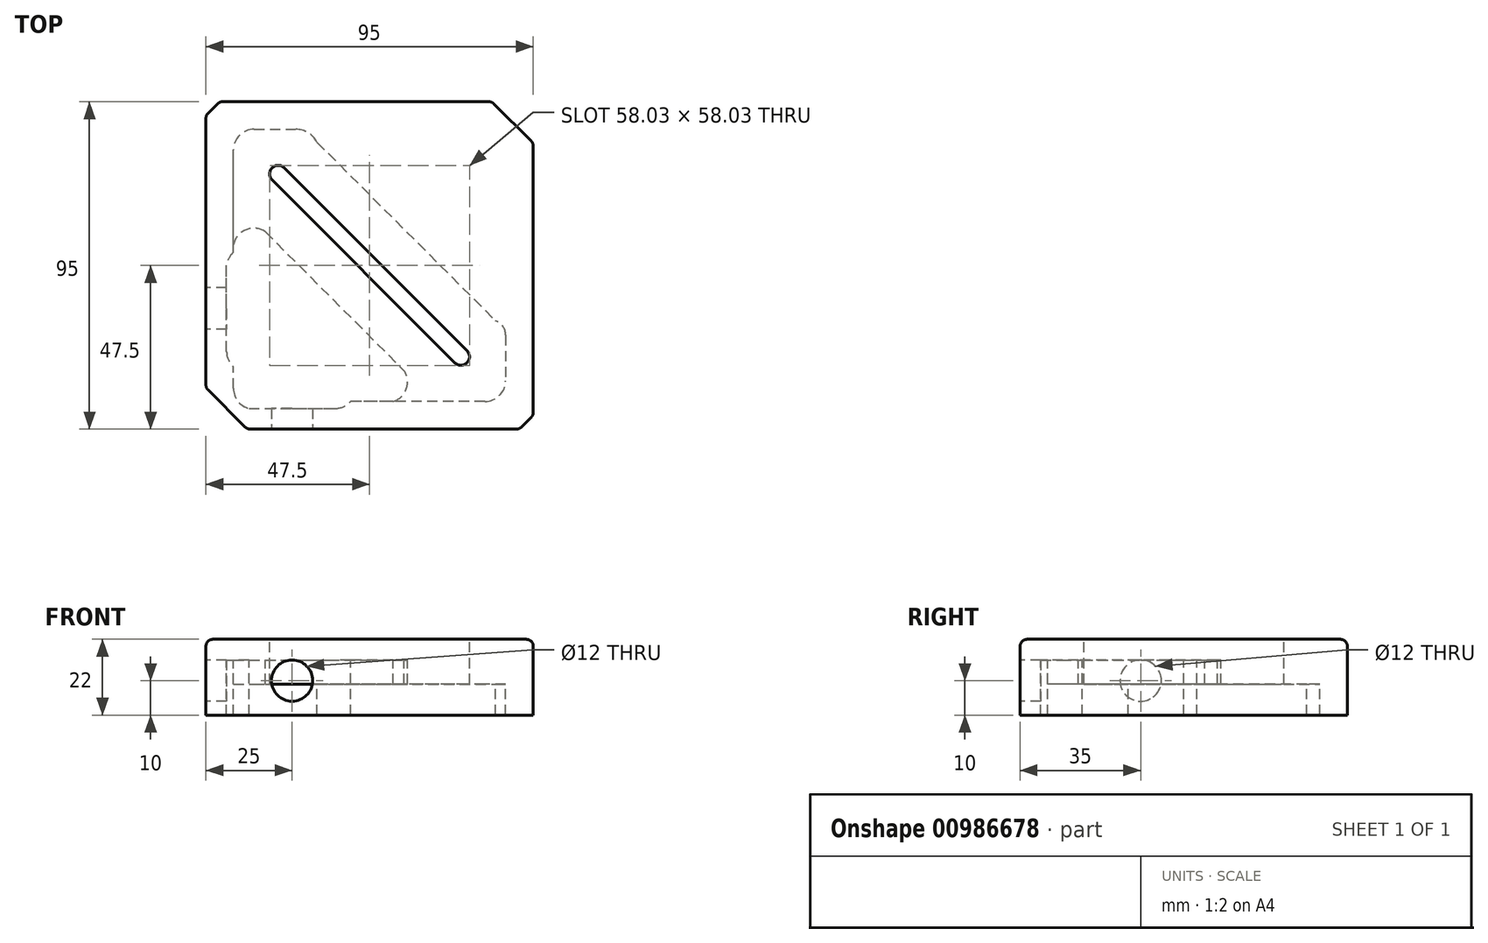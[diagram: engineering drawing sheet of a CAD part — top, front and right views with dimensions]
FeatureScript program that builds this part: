
annotation { "Feature Type Name" : "Feature", "Feature Type Description" : "" }
export const myFeature = defineFeature(function(context is Context, id is Id, definition is map)
    precondition{}
    {
        {
            var Q0;
            Q0=qCreatedBy(makeId("Top.planeOp"),FACE);
            var sketch = newSketch(context, id + "F0", { "sketchPlane" : qUnion([Q0])});
            skLineSegment(sketch, "E0.bottom", {"start": v(4, 0) * mm, "end": v(83, 0) * mm});
            skLineSegment(sketch, "E0.top", {"start": v(12, 95) * mm, "end": v(91, 95) * mm});
            skLineSegment(sketch, "E0.left", {"start": v(0, 4) * mm, "end": v(0, 83) * mm});
            skLineSegment(sketch, "E0.right", {"start": v(95, 12) * mm, "end": v(95, 91) * mm});
            skLineSegment(sketch, "E1", {"start": v(0, 83) * mm, "end": v(12, 95) * mm});
            skLineSegment(sketch, "E2", {"start": v(95, 12) * mm, "end": v(83, 0) * mm});
            skLineSegment(sketch, "E3", {"start": v(0, 4) * mm, "end": v(4, 0) * mm});
            skLineSegment(sketch, "E4", {"start": v(91, 95) * mm, "end": v(95, 91) * mm});
            skLineSegment(sketch, "E5.left", {"start": v(75.78, 72.25) * mm, "end": v(22.75, 19.22) * mm});
            skLineSegment(sketch, "E5.right", {"start": v(72.25, 75.78) * mm, "end": v(19.22, 22.75) * mm});
            skPoint(sketch, "E5.middle", {"position": v(47.5, 47.5) * mm});
            skArc(sketch, "E6", {"start": v(75.78, 72.25) * mm, "mid": v(75.78, 75.78) * mm, "end": v(72.25, 75.78) * mm});
            skArc(sketch, "E7", {"start": v(19.22, 22.75) * mm, "mid": v(19.22, 19.22) * mm, "end": v(22.75, 19.22) * mm});
            skLineSegment(sketch, "E8", {"start": v(32.28, 11.77) * mm, "end": v(84.09, 63.58) * mm});
            skLineSegment(sketch, "E9", {"start": v(87, 67.7) * mm, "end": v(87, 81) * mm});
            skLineSegment(sketch, "E10", {"start": v(81, 87) * mm, "end": v(41.97, 87) * mm});
            skLineSegment(sketch, "E11", {"start": v(8, 83.2) * mm, "end": v(8, 76.97) * mm});
            skLineSegment(sketch, "E12", {"start": v(14, 8) * mm, "end": v(26, 8) * mm});
            skArc(sketch, "E13", {"start": v(8, 14) * mm, "mid": v(9.76, 9.76) * mm, "end": v(14, 8) * mm});
            skArc(sketch, "E14", {"start": v(87, 81) * mm, "mid": v(85.24, 85.24) * mm, "end": v(81, 87) * mm});
            skPoint(sketch, "E15.orphan", {"position": v(85, 64.5) * mm});
            skPoint(sketch, "E16.orphan", {"position": v(8, 10.07) * mm});
            skPoint(sketch, "E17.orphan", {"position": v(30.58, 10.07) * mm});
            skArc(sketch, "E18", {"start": v(84.09, 63.58) * mm, "mid": v(86.2, 65.18) * mm, "end": v(87, 67.7) * mm});
            skArc(sketch, "E19", {"start": v(26, 8) * mm, "mid": v(29.67, 9.02) * mm, "end": v(32.28, 11.77) * mm});
            skLineSegment(sketch, "E20", {"start": v(17.26, 37.76) * mm, "end": v(57.54, 78.05) * mm});
            skArc(sketch, "E21", {"start": v(8, 41.46) * mm, "mid": v(11.64, 37.14) * mm, "end": v(17.26, 37.76) * mm});
            skArc(sketch, "E22", {"start": v(57.54, 78.05) * mm, "mid": v(58.15, 83.3) * mm, "end": v(54.36, 87) * mm});
            skLineSegment(sketch, "E23", {"start": v(12.5, 89) * mm, "end": v(37.5, 89) * mm});
            skLineSegment(sketch, "E24", {"start": v(6, 72.5) * mm, "end": v(6, 47.5) * mm});
            skArc(sketch, "E25", {"start": v(12.5, 89) * mm, "mid": v(9.26, 86.86) * mm, "end": v(8, 83.2) * mm});
            skArc(sketch, "E26", {"start": v(41.97, 87) * mm, "mid": v(39.95, 88.48) * mm, "end": v(37.5, 89) * mm});
            skArc(sketch, "E27", {"start": v(8, 76.97) * mm, "mid": v(6.52, 74.95) * mm, "end": v(6, 72.5) * mm});
            skArc(sketch, "E28", {"start": v(6, 47.5) * mm, "mid": v(6.64, 45.4) * mm, "end": v(8, 43.66) * mm});
            skPoint(sketch, "E29.start.orphan", {"position": v(25, 89) * mm});
            skPoint(sketch, "E30.start.orphan", {"position": v(6, 60) * mm});
            skLineSegment(sketch, "E31.trimOffspring", {"start": v(8, 43.66) * mm, "end": v(8, 14) * mm});
            skSolve(sketch);
        }
        {
            var Q0;
            Q0=makeQuery(id+"F0.imprint","IMPRINT",FACE,{"disambiguationData":[TD([[makeQuery(id+"F0.imprint","IMPRINT",EDGE,{"derivedFrom":sQuery(id+"F0.wireOp",EDGE,"E5.left")}),1.0]])]});
            extrude(context, id + "F1", {"entities" : qUnion([Q0]), "depth" : 13 * mm, "offsetDistance" : 25 * mm});
        }
        {
            var Q0;
            Q0=makeQuery(id+"F0.imprint","IMPRINT",FACE,{"disambiguationData":[TD([[makeQuery(id+"F0.imprint","IMPRINT",EDGE,{"derivedFrom":sQuery(id+"F0.wireOp",EDGE,"E0.bottom")}),1.0]])]});
            extrude(context, id + "F2", {"entities" : qUnion([Q0]), "operationType" : NewBodyOperationType.ADD, "depth" : 22 * mm, "offsetDistance" : 25 * mm});
        }
        {
            var Q0;
            Q0=makeQuery(id+"F0.imprint","IMPRINT",FACE,{"disambiguationData":[TD([[makeQuery(id+"F0.imprint","IMPRINT",EDGE,{"derivedFrom":sQuery(id+"F0.wireOp",EDGE,"E11")}),1.0]])]});
            extrude(context, id + "F3", {"entities" : qUnion([Q0]), "operationType" : NewBodyOperationType.ADD, "depth" : 6 * mm, "offsetDistance" : 25 * mm});
        }
        {
            var Q0;
            Q0=makeQuery(id+"F2.opExtrude","CAP_EDGE",EDGE,{"disambiguationData":[OSD([sQuery(id+"F0.wireOp",EDGE,"E0.top")])],"isStart":true});
            var Q1;
            Q1=makeQuery(id+"F2.opExtrude","SWEPT_EDGE",EDGE,{"disambiguationData":[OSD([sQuery(id+"F0.wireOp",EDGE,"E0.top"),sQuery(id+"F0.wireOp",EDGE,"E4")])]});
            var Q2;
            Q2=makeQuery(id+"F2.opExtrude","SWEPT_EDGE",EDGE,{"disambiguationData":[OSD([sQuery(id+"F0.wireOp",EDGE,"E0.right"),sQuery(id+"F0.wireOp",EDGE,"E4")])]});
            var Q3;
            Q3=makeQuery(id+"F2.opExtrude","CAP_EDGE",EDGE,{"disambiguationData":[OSD([sQuery(id+"F0.wireOp",EDGE,"E0.right")])],"isStart":true});
            var Q4;
            Q4=makeQuery(id+"F2.opExtrude","CAP_EDGE",EDGE,{"disambiguationData":[OSD([sQuery(id+"F0.wireOp",EDGE,"E4")])],"isStart":true});
            var Q5;
            Q5=makeQuery(id+"F2.opExtrude","CAP_EDGE",EDGE,{"disambiguationData":[OSD([sQuery(id+"F0.wireOp",EDGE,"E2")])],"isStart":true});
            var Q6;
            Q6=makeQuery(id+"F2.opExtrude","SWEPT_EDGE",EDGE,{"disambiguationData":[OSD([sQuery(id+"F0.wireOp",EDGE,"E0.bottom"),sQuery(id+"F0.wireOp",EDGE,"E2")])]});
            var Q7;
            Q7=makeQuery(id+"F2.opExtrude","SWEPT_EDGE",EDGE,{"disambiguationData":[OSD([sQuery(id+"F0.wireOp",EDGE,"E0.right"),sQuery(id+"F0.wireOp",EDGE,"E2")])]});
            var Q8;
            Q8=makeQuery(id+"F2.opExtrude","CAP_EDGE",EDGE,{"disambiguationData":[OSD([sQuery(id+"F0.wireOp",EDGE,"E0.bottom")])],"isStart":true});
            var Q9;
            Q9=makeQuery(id+"F2.opExtrude","SWEPT_EDGE",EDGE,{"disambiguationData":[OSD([sQuery(id+"F0.wireOp",EDGE,"E0.bottom"),sQuery(id+"F0.wireOp",EDGE,"E3")])]});
            var Q10;
            Q10=makeQuery(id+"F2.opExtrude","CAP_EDGE",EDGE,{"disambiguationData":[OSD([sQuery(id+"F0.wireOp",EDGE,"E3")])],"isStart":true});
            var Q11;
            Q11=makeQuery(id+"F2.opExtrude","SWEPT_EDGE",EDGE,{"disambiguationData":[OSD([sQuery(id+"F0.wireOp",EDGE,"E0.left"),sQuery(id+"F0.wireOp",EDGE,"E3")])]});
            var Q12;
            Q12=makeQuery(id+"F2.opExtrude","CAP_EDGE",EDGE,{"disambiguationData":[OSD([sQuery(id+"F0.wireOp",EDGE,"E0.left")])],"isStart":true});
            var Q13;
            Q13=makeQuery(id+"F2.opExtrude","CAP_EDGE",EDGE,{"disambiguationData":[OSD([sQuery(id+"F0.wireOp",EDGE,"E1")])],"isStart":true});
            var Q14;
            Q14=makeQuery(id+"F2.opExtrude","SWEPT_EDGE",EDGE,{"disambiguationData":[OSD([sQuery(id+"F0.wireOp",EDGE,"E0.left"),sQuery(id+"F0.wireOp",EDGE,"E1")])]});
            var Q15;
            Q15=makeQuery(id+"F2.opExtrude","SWEPT_EDGE",EDGE,{"disambiguationData":[OSD([sQuery(id+"F0.wireOp",EDGE,"E0.top"),sQuery(id+"F0.wireOp",EDGE,"E1")])]});
            fillet(context, id + "F4", {"entities" : qUnion([Q0, Q1, Q2, Q3, Q4, Q5, Q6, Q7, Q8, Q9, Q10, Q11, Q12, Q13, Q14, Q15]), "radius" : 2 * mm, "tangentPropagation" : true, "allowEdgeOverflow" : false});
        }
        {
            var Q0;
            Q0=makeQuery(id+"F2.opExtrude","SWEPT_FACE",FACE,{"disambiguationData":[OSD([sQuery(id+"F0.wireOp",EDGE,"E0.left")])]});
            var sketch = newSketch(context, id + "F5", { "sketchPlane" : qUnion([Q0])});
            skCircle(sketch, "E32", {"center": v(-60, 12) * mm, "radius": 6 * mm});
            skPoint(sketch, "E33", {"position": v(-82.17, 12) * mm});
            skSolve(sketch);
        }
        {
            var Q0;
            Q0=sQuery(id+"F5.wireOp",VERTEX,"E32.center");
            var Q1;
            Q1=makeQuery(id+"F1.opExtrude","SWEPT_BODY",BODY,{"disambiguationData":[OSD([sQuery(id+"F0.wireOp",EDGE,"E5.left"),sQuery(id+"F0.wireOp",EDGE,"E5.right"),sQuery(id+"F0.wireOp",EDGE,"E6"),sQuery(id+"F0.wireOp",EDGE,"E7"),sQuery(id+"F0.wireOp",EDGE,"E8"),sQuery(id+"F0.wireOp",EDGE,"E9"),sQuery(id+"F0.wireOp",EDGE,"E10"),sQuery(id+"F0.wireOp",EDGE,"E11"),sQuery(id+"F0.wireOp",EDGE,"E12"),sQuery(id+"F0.wireOp",EDGE,"E13"),sQuery(id+"F0.wireOp",EDGE,"E14"),sQuery(id+"F0.wireOp",EDGE,"dTPDkBi0-P8Fg-LGXg-OxUh-iqolI7d0LJ0Z"),sQuery(id+"F0.wireOp",EDGE,"AbjG9SvJ-RGuI-1kTg-4pos-58oHFgegNcMA"),sQuery(id+"F0.wireOp",EDGE,"7NH4ejp4-lPfR-9Dju-DP9M-AQ5HTiFhW5h4")])]});
            hole(context, id + "F6", {"style" : HoleStyle.SIMPLE, "endStyle" : HoleEndStyle.BLIND, "holeDiameter" : 12 * mm, "majorDiameter" : 5 * mm, "holeDepth" : 32 * mm, "isTappedThrough" : true, "tappedDepth" : 12 * mm, "tapClearance" : 3, "locations" : qUnion([Q0]), "scope" : qUnion([Q1])});
        }
        {
            var Q0;
            Q0=makeQuery(id+"F1.opExtrude","SWEPT_BODY",BODY,{"disambiguationData":[OSD([sQuery(id+"F0.wireOp",EDGE,"E5.left"),sQuery(id+"F0.wireOp",EDGE,"E5.right"),sQuery(id+"F0.wireOp",EDGE,"E6"),sQuery(id+"F0.wireOp",EDGE,"E7"),sQuery(id+"F0.wireOp",EDGE,"E8"),sQuery(id+"F0.wireOp",EDGE,"E9"),sQuery(id+"F0.wireOp",EDGE,"E10"),sQuery(id+"F0.wireOp",EDGE,"E11"),sQuery(id+"F0.wireOp",EDGE,"E12"),sQuery(id+"F0.wireOp",EDGE,"E13"),sQuery(id+"F0.wireOp",EDGE,"E14"),sQuery(id+"F0.wireOp",EDGE,"dTPDkBi0-P8Fg-LGXg-OxUh-iqolI7d0LJ0Z"),sQuery(id+"F0.wireOp",EDGE,"AbjG9SvJ-RGuI-1kTg-4pos-58oHFgegNcMA"),sQuery(id+"F0.wireOp",EDGE,"7NH4ejp4-lPfR-9Dju-DP9M-AQ5HTiFhW5h4")])]});
            var Q1;
            Q1=makeQuery(id+"F3.opExtrude","SWEPT_BODY",BODY,{"disambiguationData":[OSD([sQuery(id+"F0.wireOp",EDGE,"E10"),sQuery(id+"F0.wireOp",EDGE,"E11"),sQuery(id+"F0.wireOp",EDGE,"7NH4ejp4-lPfR-9Dju-DP9M-AQ5HTiFhW5h4"),sQuery(id+"F0.wireOp",EDGE,"E20"),sQuery(id+"F0.wireOp",EDGE,"E21"),sQuery(id+"F0.wireOp",EDGE,"E22")])]});
            var Q2;
            {var subQ0=sQuery(id+"F0.wireOp",EDGE,"7NH4ejp4-lPfR-9Dju-DP9M-AQ5HTiFhW5h4");var subQ1=sQuery(id+"F0.wireOp",EDGE,"AbjG9SvJ-RGuI-1kTg-4pos-58oHFgegNcMA");var subQ2=sQuery(id+"F0.wireOp",EDGE,"dTPDkBi0-P8Fg-LGXg-OxUh-iqolI7d0LJ0Z");var subQ3=sQuery(id+"F0.wireOp",EDGE,"E14");var subQ4=sQuery(id+"F0.wireOp",EDGE,"E13");var subQ5=sQuery(id+"F0.wireOp",EDGE,"E12");var subQ6=sQuery(id+"F0.wireOp",EDGE,"E11");var subQ7=sQuery(id+"F0.wireOp",EDGE,"E10");var subQ8=sQuery(id+"F0.wireOp",EDGE,"E9");var subQ9=sQuery(id+"F0.wireOp",EDGE,"E8");var subQ10=sQuery(id+"F0.wireOp",EDGE,"E0.bottom");Q2=makeQuery(id+"F4.opFillet","BLEND_EDGE",EDGE,{"blendedFrom":[makeQuery(id+"F2.opExtrude","CAP_EDGE",EDGE,{"disambiguationData":[OSD([subQ10])],"isStart":true}),makeQuery(id+"F2.boolean.opBoolean","MERGE",FACE,{"derivedFrom":[makeQuery(id+"F1.opExtrude","CAP_FACE",FACE,{"disambiguationData":[OSD([sQuery(id+"F0.wireOp",EDGE,"E5.left"),sQuery(id+"F0.wireOp",EDGE,"E5.right"),sQuery(id+"F0.wireOp",EDGE,"E6"),sQuery(id+"F0.wireOp",EDGE,"E7"),subQ9,subQ8,subQ7,subQ6,subQ5,subQ4,subQ3,subQ2,subQ1,subQ0])],"isStart":true}),makeQuery(id+"F2.opExtrude","CAP_FACE",FACE,{"disambiguationData":[OSD([subQ10,sQuery(id+"F0.wireOp",EDGE,"E0.top"),sQuery(id+"F0.wireOp",EDGE,"E0.left"),sQuery(id+"F0.wireOp",EDGE,"E0.right"),sQuery(id+"F0.wireOp",EDGE,"E1"),sQuery(id+"F0.wireOp",EDGE,"E2"),sQuery(id+"F0.wireOp",EDGE,"E3"),sQuery(id+"F0.wireOp",EDGE,"E4"),subQ9,subQ8,subQ7,subQ6,subQ5,subQ4,subQ3,subQ2,subQ1,subQ0])],"isStart":true})]})],"blendedInto":[makeQuery(id+"F2.boolean.opBoolean","MERGE",FACE,{"derivedFrom":[makeQuery(id+"F1.opExtrude","CAP_FACE",FACE,{"disambiguationData":[OSD([sQuery(id+"F0.wireOp",EDGE,"E5.left"),sQuery(id+"F0.wireOp",EDGE,"E5.right"),sQuery(id+"F0.wireOp",EDGE,"E6"),sQuery(id+"F0.wireOp",EDGE,"E7"),subQ9,subQ8,subQ7,subQ6,subQ5,subQ4,subQ3,subQ2,subQ1,subQ0])],"isStart":true}),makeQuery(id+"F2.opExtrude","CAP_FACE",FACE,{"disambiguationData":[OSD([subQ10,sQuery(id+"F0.wireOp",EDGE,"E0.top"),sQuery(id+"F0.wireOp",EDGE,"E0.left"),sQuery(id+"F0.wireOp",EDGE,"E0.right"),sQuery(id+"F0.wireOp",EDGE,"E1"),sQuery(id+"F0.wireOp",EDGE,"E2"),sQuery(id+"F0.wireOp",EDGE,"E3"),sQuery(id+"F0.wireOp",EDGE,"E4"),subQ9,subQ8,subQ7,subQ6,subQ5,subQ4,subQ3,subQ2,subQ1,subQ0])],"isStart":true})]})]});}
            transform(context, id + "F7", {"entities" : qUnion([Q0, Q1]), "transformType" : TransformType.ROTATION, "transformAxis" : qUnion([Q2]), "angle" : 180 * degree, "makeCopy" : false});
        }
        {
            var Q0;
            Q0=makeQuery(id+"F2.opExtrude","SWEPT_FACE",FACE,{"disambiguationData":[OSD([sQuery(id+"F0.wireOp",EDGE,"E0.top")])]});
            var sketch = newSketch(context, id + "F8", { "sketchPlane" : qUnion([Q0])});
            skCircle(sketch, "E34", {"center": v(25, -12) * mm, "radius": 6 * mm});
            skPoint(sketch, "E35", {"position": v(12.83, -12) * mm});
            skSolve(sketch);
        }
        {
            var Q0;
            Q0=sQuery(id+"F8.wireOp",VERTEX,"E34.center");
            var Q1;
            Q1=makeQuery(id+"F1.opExtrude","SWEPT_BODY",BODY,{"disambiguationData":[OSD([sQuery(id+"F0.wireOp",EDGE,"E5.left"),sQuery(id+"F0.wireOp",EDGE,"E5.right"),sQuery(id+"F0.wireOp",EDGE,"E6"),sQuery(id+"F0.wireOp",EDGE,"E7"),sQuery(id+"F0.wireOp",EDGE,"E8"),sQuery(id+"F0.wireOp",EDGE,"E9"),sQuery(id+"F0.wireOp",EDGE,"E10"),sQuery(id+"F0.wireOp",EDGE,"E11"),sQuery(id+"F0.wireOp",EDGE,"E12"),sQuery(id+"F0.wireOp",EDGE,"E13"),sQuery(id+"F0.wireOp",EDGE,"E14"),sQuery(id+"F0.wireOp",EDGE,"7NH4ejp4-lPfR-9Dju-DP9M-AQ5HTiFhW5h4"),sQuery(id+"F0.wireOp",EDGE,"E18"),sQuery(id+"F0.wireOp",EDGE,"E19")])]});
            hole(context, id + "F9", {"style" : HoleStyle.SIMPLE, "endStyle" : HoleEndStyle.BLIND, "holeDiameter" : 12 * mm, "majorDiameter" : 5 * mm, "holeDepth" : 35 * mm, "isTappedThrough" : true, "tappedDepth" : 12 * mm, "tapClearance" : 3, "locations" : qUnion([Q0]), "scope" : qUnion([Q1])});
        }
    });
